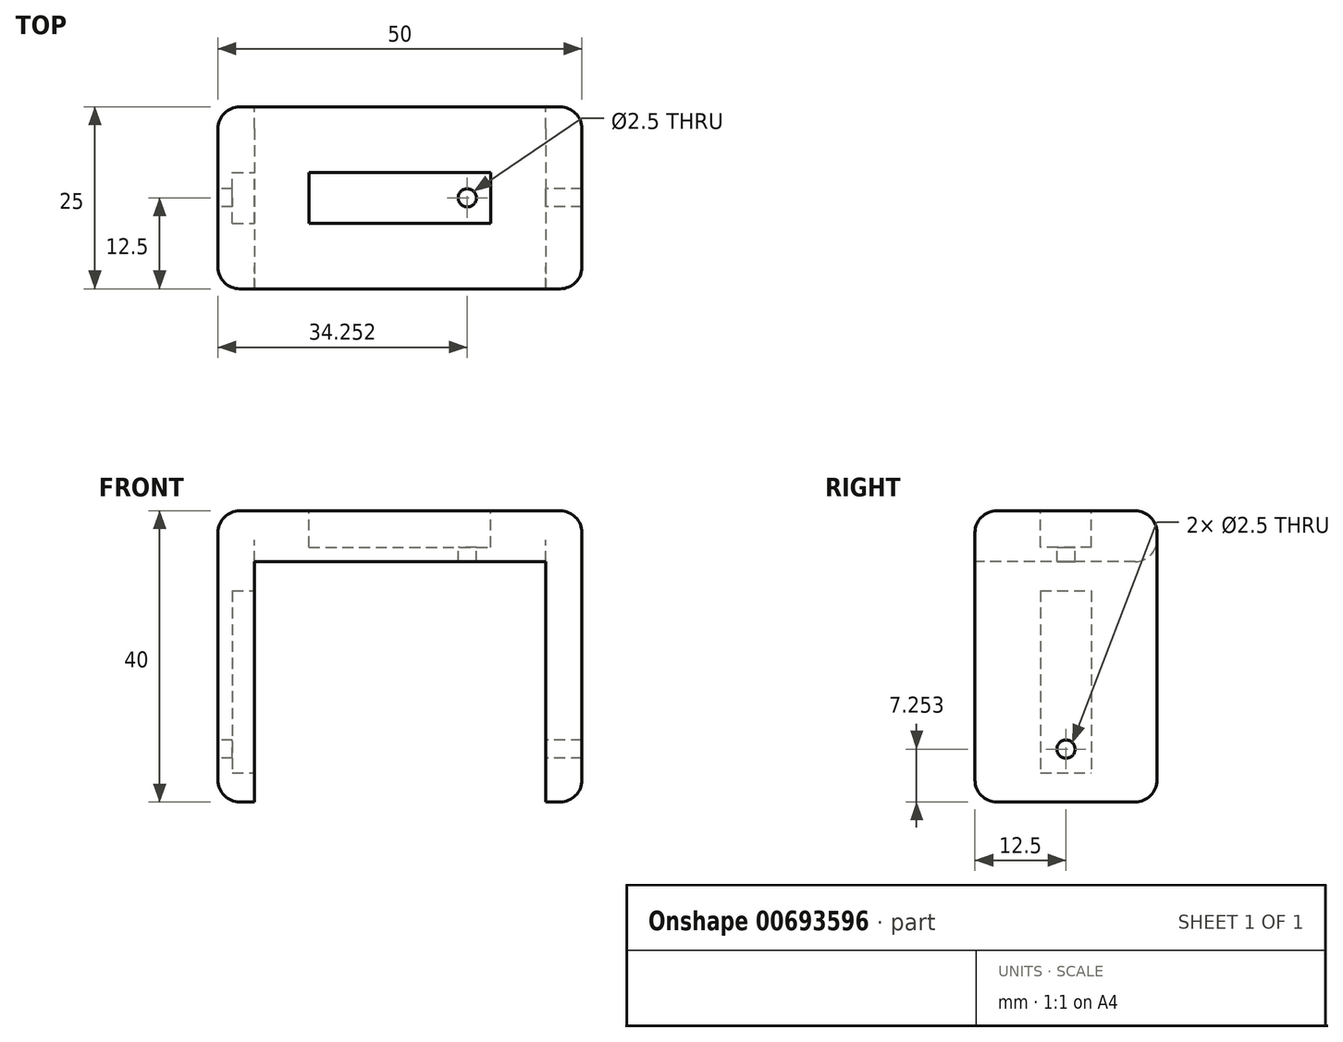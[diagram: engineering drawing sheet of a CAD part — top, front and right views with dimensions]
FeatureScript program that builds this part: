
annotation { "Feature Type Name" : "Feature", "Feature Type Description" : "" }
export const myFeature = defineFeature(function(context is Context, id is Id, definition is map)
    precondition{}
    {
        {
            var Q0;
            Q0=qCreatedBy(makeId("Front.planeOp"),FACE);
            var sketch = newSketch(context, id + "F0", { "sketchPlane" : qUnion([Q0])});
            skLineSegment(sketch, "E0.bottom", {"start": v(-21, 25.16) * mm, "end": v(29, 25.16) * mm});
            skLineSegment(sketch, "E0.top", {"start": v(-21, -14.84) * mm, "end": v(29, -14.84) * mm});
            skLineSegment(sketch, "E0.left", {"start": v(-21, 25.16) * mm, "end": v(-21, -14.84) * mm});
            skLineSegment(sketch, "E0.right", {"start": v(29, 25.16) * mm, "end": v(29, -14.84) * mm});
            skSolve(sketch);
        }
        {
            var Q0;
            Q0 = qSketchRegion(id + "F0", true);
            extrude(context, id + "F1", {"entities" : qUnion([Q0]), "depth" : 25 * mm, "offsetDistance" : 25 * mm});
        }
        {
            var Q0;
            Q0=makeQuery(id+"F1.opExtrude","CAP_FACE",FACE,{"disambiguationData":[OSD([sQuery(id+"F0.wireOp",EDGE,"E0.bottom"),sQuery(id+"F0.wireOp",EDGE,"E0.top"),sQuery(id+"F0.wireOp",EDGE,"E0.left"),sQuery(id+"F0.wireOp",EDGE,"E0.right")])],"isStart":false});
            var sketch = newSketch(context, id + "F2", { "sketchPlane" : qUnion([Q0])});
            skLineSegment(sketch, "E1.bottom", {"start": v(24, -14.84) * mm, "end": v(-16, -14.84) * mm});
            skLineSegment(sketch, "E1.top", {"start": v(24, 18.16) * mm, "end": v(-16, 18.16) * mm});
            skLineSegment(sketch, "E1.left", {"start": v(24, -14.84) * mm, "end": v(24, 18.16) * mm});
            skLineSegment(sketch, "E1.right", {"start": v(-16, -14.84) * mm, "end": v(-16, 18.16) * mm});
            skSolve(sketch);
        }
        {
            var Q0;
            Q0 = qSketchRegion(id + "F2", true);
            extrude(context, id + "F3", {"entities" : qUnion([Q0]), "operationType" : NewBodyOperationType.REMOVE, "endBound" : BoundingType.THROUGH_ALL, "oppositeDirection" : true, "depth" : 25 * mm, "offsetDistance" : 25 * mm});
        }
        {
            var Q0;
            Q0=makeQuery(id+"F3.boolean.opBoolean","COPY",FACE,{"derivedFrom":makeQuery(id+"F3.opExtrude","SWEPT_FACE",FACE,{"disambiguationData":[OSD([sQuery(id+"F2.wireOp",EDGE,"E1.right")])]})});
            var sketch = newSketch(context, id + "F4", { "sketchPlane" : qUnion([Q0])});
            skLineSegment(sketch, "E2.bottom", {"start": v(-16, 14.16) * mm, "end": v(-9, 14.16) * mm});
            skLineSegment(sketch, "E2.top", {"start": v(-16, -10.84) * mm, "end": v(-9, -10.84) * mm});
            skLineSegment(sketch, "E2.left", {"start": v(-16, 14.16) * mm, "end": v(-16, -10.84) * mm});
            skLineSegment(sketch, "E2.right", {"start": v(-9, 14.16) * mm, "end": v(-9, -10.84) * mm});
            skSolve(sketch);
        }
        {
            var Q0;
            Q0 = qSketchRegion(id + "F4", true);
            extrude(context, id + "F5", {"entities" : qUnion([Q0]), "operationType" : NewBodyOperationType.REMOVE, "oppositeDirection" : true, "depth" : 3 * mm, "offsetDistance" : 25 * mm});
        }
        {
            var Q0;
            Q0=makeQuery(id+"F1.opExtrude","SWEPT_FACE",FACE,{"disambiguationData":[OSD([sQuery(id+"F0.wireOp",EDGE,"E0.left")])]});
            var sketch = newSketch(context, id + "F6", { "sketchPlane" : qUnion([Q0])});
            skCircle(sketch, "E3", {"center": v(12.5, -7.59) * mm, "radius": 1.25 * mm});
            skSolve(sketch);
        }
        {
            var Q0;
            Q0 = qSketchRegion(id + "F6", true);
            extrude(context, id + "F7", {"entities" : qUnion([Q0]), "operationType" : NewBodyOperationType.REMOVE, "endBound" : BoundingType.THROUGH_ALL, "oppositeDirection" : true, "depth" : 25 * mm, "offsetDistance" : 25 * mm});
        }
        {
            var Q0;
            Q0=makeQuery(id+"F1.opExtrude","SWEPT_FACE",FACE,{"disambiguationData":[OSD([sQuery(id+"F0.wireOp",EDGE,"E0.bottom")])]});
            var sketch = newSketch(context, id + "F8", { "sketchPlane" : qUnion([Q0])});
            skLineSegment(sketch, "E4.bottom", {"start": v(-8.5, -9) * mm, "end": v(16.5, -9) * mm});
            skLineSegment(sketch, "E4.top", {"start": v(-8.5, -16) * mm, "end": v(16.5, -16) * mm});
            skLineSegment(sketch, "E4.left", {"start": v(-8.5, -9) * mm, "end": v(-8.5, -16) * mm});
            skLineSegment(sketch, "E4.right", {"start": v(16.5, -9) * mm, "end": v(16.5, -16) * mm});
            skSolve(sketch);
        }
        {
            var Q0;
            Q0 = qSketchRegion(id + "F8", true);
            extrude(context, id + "F9", {"entities" : qUnion([Q0]), "operationType" : NewBodyOperationType.REMOVE, "oppositeDirection" : true, "depth" : 5 * mm, "offsetDistance" : 25 * mm});
        }
        {
            var Q0;
            Q0=makeQuery(id+"F9.boolean.opBoolean","COPY",FACE,{"derivedFrom":makeQuery(id+"F9.opExtrude","CAP_FACE",FACE,{"disambiguationData":[OSD([sQuery(id+"F8.wireOp",EDGE,"E4.bottom"),sQuery(id+"F8.wireOp",EDGE,"E4.top"),sQuery(id+"F8.wireOp",EDGE,"E4.left"),sQuery(id+"F8.wireOp",EDGE,"E4.right")])],"isStart":false})});
            var sketch = newSketch(context, id + "F10", { "sketchPlane" : qUnion([Q0])});
            skCircle(sketch, "E5", {"center": v(13.25, -12.5) * mm, "radius": 1.25 * mm});
            skSolve(sketch);
        }
        {
            var Q0;
            Q0 = qSketchRegion(id + "F10", true);
            extrude(context, id + "F11", {"entities" : qUnion([Q0]), "operationType" : NewBodyOperationType.REMOVE, "oppositeDirection" : true, "depth" : 2 * mm, "offsetDistance" : 25 * mm});
        }
        {
            var Q0;
            Q0=makeQuery(id+"F1.opExtrude","SWEPT_EDGE",EDGE,{"disambiguationData":[OSD([sQuery(id+"F0.wireOp",EDGE,"E0.bottom"),sQuery(id+"F0.wireOp",EDGE,"E0.right")])]});
            var Q1;
            Q1=makeQuery(id+"F1.opExtrude","SWEPT_EDGE",EDGE,{"disambiguationData":[OSD([sQuery(id+"F0.wireOp",EDGE,"E0.bottom"),sQuery(id+"F0.wireOp",EDGE,"E0.left")])]});
            var Q2;
            Q2=makeQuery(id+"F1.opExtrude","CAP_EDGE",EDGE,{"disambiguationData":[OSD([sQuery(id+"F0.wireOp",EDGE,"E0.bottom")])],"isStart":true});
            var Q3;
            Q3=makeQuery(id+"F1.opExtrude","CAP_EDGE",EDGE,{"disambiguationData":[OSD([sQuery(id+"F0.wireOp",EDGE,"E0.bottom")])],"isStart":false});
            var Q4;
            Q4=makeQuery(id+"F1.opExtrude","CAP_EDGE",EDGE,{"disambiguationData":[OSD([sQuery(id+"F0.wireOp",EDGE,"E0.right")])],"isStart":false});
            var Q5;
            Q5=makeQuery(id+"F1.opExtrude","CAP_EDGE",EDGE,{"disambiguationData":[OSD([sQuery(id+"F0.wireOp",EDGE,"E0.right")])],"isStart":true});
            var Q6;
            Q6=makeQuery(id+"F1.opExtrude","CAP_EDGE",EDGE,{"disambiguationData":[OSD([sQuery(id+"F0.wireOp",EDGE,"E0.left")])],"isStart":false});
            var Q7;
            Q7=makeQuery(id+"F1.opExtrude","CAP_EDGE",EDGE,{"disambiguationData":[OSD([sQuery(id+"F0.wireOp",EDGE,"E0.left")])],"isStart":true});
            var Q8;
            Q8=makeQuery(id+"F1.opExtrude","SWEPT_EDGE",EDGE,{"disambiguationData":[OSD([sQuery(id+"F0.wireOp",EDGE,"E0.top"),sQuery(id+"F0.wireOp",EDGE,"E0.left")])]});
            var Q9;
            Q9=makeQuery(id+"F1.opExtrude","SWEPT_EDGE",EDGE,{"disambiguationData":[OSD([sQuery(id+"F0.wireOp",EDGE,"E0.top"),sQuery(id+"F0.wireOp",EDGE,"E0.right")])]});
            var Q10;
            {var subQ0=sQuery(id+"F0.wireOp",EDGE,"E0.left");var subQ1=sQuery(id+"F0.wireOp",EDGE,"E0.top");Q10=makeQuery(id+"F3.boolean.opBoolean","SPLIT",EDGE,{"disambiguationData":[TD([makeQuery(id+"F1.opExtrude","SWEPT_FACE",FACE,{"disambiguationData":[OSD([subQ0])]})])],"derivedFrom":makeQuery(id+"F1.opExtrude","CAP_EDGE",EDGE,{"disambiguationData":[OSD([subQ1])],"isStart":false})});}
            var Q11;
            {var subQ0=sQuery(id+"F0.wireOp",EDGE,"E0.left");var subQ1=sQuery(id+"F0.wireOp",EDGE,"E0.top");Q11=makeQuery(id+"F3.boolean.opBoolean","SPLIT",EDGE,{"disambiguationData":[TD([makeQuery(id+"F1.opExtrude","SWEPT_FACE",FACE,{"disambiguationData":[OSD([subQ0])]})])],"derivedFrom":makeQuery(id+"F1.opExtrude","CAP_EDGE",EDGE,{"disambiguationData":[OSD([subQ1])],"isStart":true})});}
            var Q12;
            {var subQ0=sQuery(id+"F0.wireOp",EDGE,"E0.right");var subQ1=sQuery(id+"F0.wireOp",EDGE,"E0.top");Q12=makeQuery(id+"F3.boolean.opBoolean","SPLIT",EDGE,{"disambiguationData":[TD([makeQuery(id+"F1.opExtrude","SWEPT_FACE",FACE,{"disambiguationData":[OSD([subQ0])]})])],"derivedFrom":makeQuery(id+"F1.opExtrude","CAP_EDGE",EDGE,{"disambiguationData":[OSD([subQ1])],"isStart":true})});}
            var Q13;
            {var subQ0=sQuery(id+"F0.wireOp",EDGE,"E0.right");var subQ1=sQuery(id+"F0.wireOp",EDGE,"E0.top");Q13=makeQuery(id+"F3.boolean.opBoolean","SPLIT",EDGE,{"disambiguationData":[TD([makeQuery(id+"F1.opExtrude","SWEPT_FACE",FACE,{"disambiguationData":[OSD([subQ0])]})])],"derivedFrom":makeQuery(id+"F1.opExtrude","CAP_EDGE",EDGE,{"disambiguationData":[OSD([subQ1])],"isStart":false})});}
            var Q14;
            Q14=makeQuery(id+"F3.boolean.opBoolean","COPY",EDGE,{"derivedFrom":makeQuery(id+"F3.opExtrude","CAP_EDGE",EDGE,{"disambiguationData":[OSD([sQuery(id+"F2.wireOp",EDGE,"E1.top")])],"isStart":true})});
            var Q15;
            Q15=makeQuery(id+"F3.boolean.opBoolean","INTERSECT",EDGE,{"derivedFrom":[makeQuery(id+"F1.opExtrude","CAP_FACE",FACE,{"disambiguationData":[OSD([sQuery(id+"F0.wireOp",EDGE,"E0.bottom"),sQuery(id+"F0.wireOp",EDGE,"E0.top"),sQuery(id+"F0.wireOp",EDGE,"E0.left"),sQuery(id+"F0.wireOp",EDGE,"E0.right")])],"isStart":true}),makeQuery(id+"F3.opExtrude","SWEPT_FACE",FACE,{"disambiguationData":[OSD([sQuery(id+"F2.wireOp",EDGE,"E1.top")])]})]});
            fillet(context, id + "F12", {"entities" : qUnion([Q0, Q1, Q2, Q3, Q4, Q5, Q6, Q7, Q8, Q9, Q10, Q11, Q12, Q13, Q14, Q15]), "radius" : 3 * mm, "tangentPropagation" : true, "allowEdgeOverflow" : false});
        }
    });
